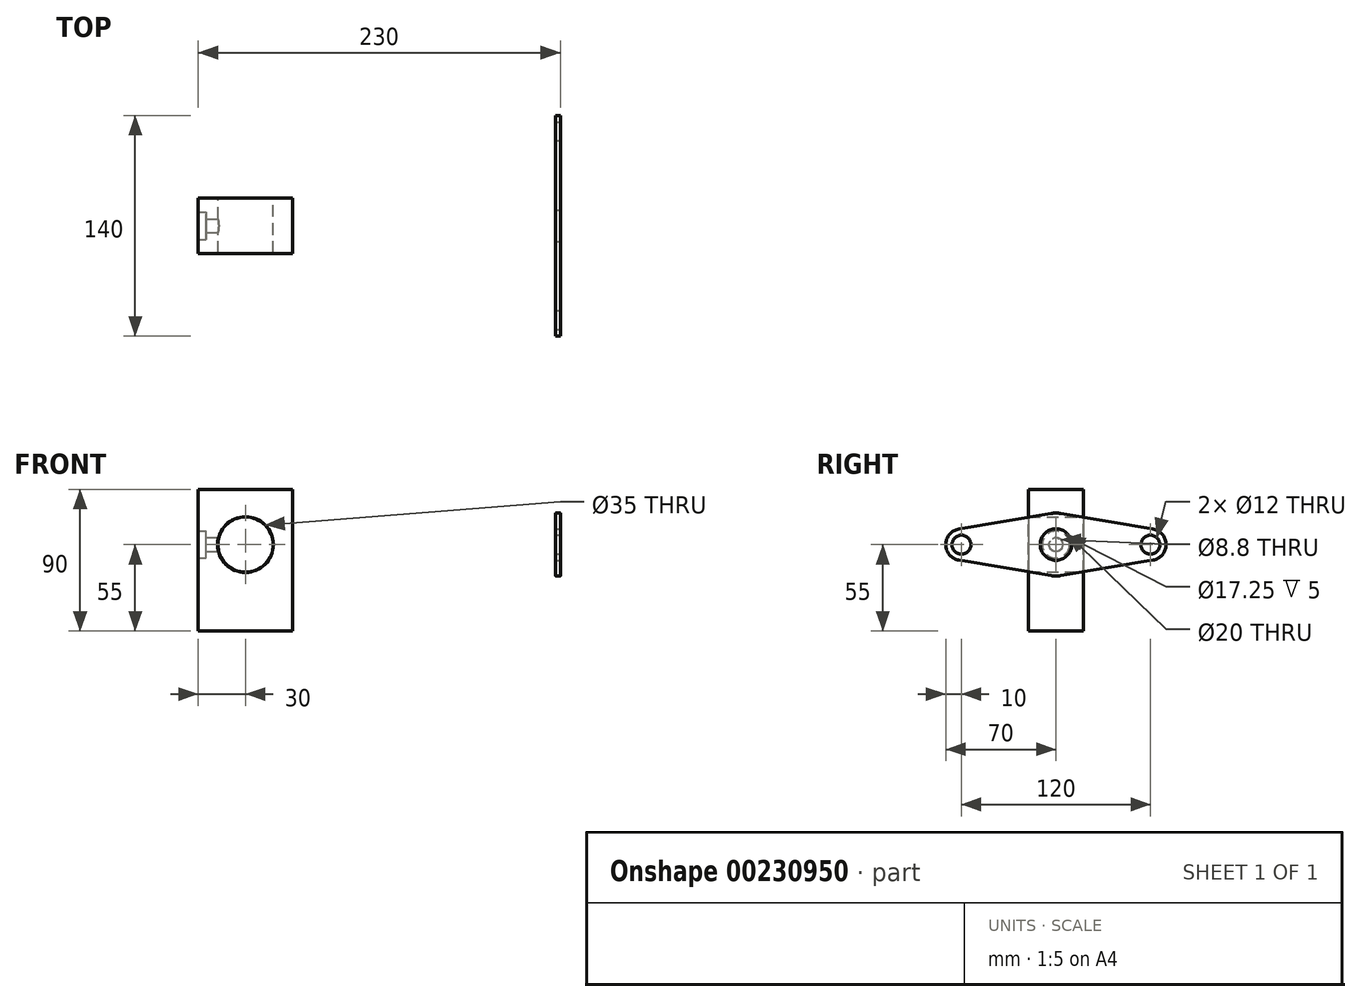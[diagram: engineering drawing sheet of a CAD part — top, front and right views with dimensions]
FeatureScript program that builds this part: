
annotation { "Feature Type Name" : "Feature", "Feature Type Description" : "" }
export const myFeature = defineFeature(function(context is Context, id is Id, definition is map)
    precondition{}
    {
        {
            var Q0;
            Q0=qCreatedBy(makeId("Front.planeOp"),FACE);
            var sketch = newSketch(context, id + "F0", { "sketchPlane" : qUnion([Q0])});
            skCircle(sketch, "E0", {"center": v(0, 0) * mm, "radius": 125 * mm, "construction": true});
            skLineSegment(sketch, "E1", {"start": v(-224.12, 0) * mm, "end": v(217.68, 0) * mm, "construction": true});
            skLineSegment(sketch, "E2", {"start": v(-200, 15.88) * mm, "end": v(-200, -15.88) * mm, "construction": true});
            skLineSegment(sketch, "E3", {"start": v(200, 15.88) * mm, "end": v(200, -15.88) * mm, "construction": true});
            skCircle(sketch, "E4", {"center": v(-200, 0) * mm, "radius": 17.5 * mm});
            skPoint(sketch, "E4.centerSnap0", {"position": v(-200, 0) * mm});
            skLineSegment(sketch, "E5.bottom", {"start": v(-230, 35) * mm, "end": v(-170, 35) * mm});
            skLineSegment(sketch, "E5.top", {"start": v(-230, -55) * mm, "end": v(-170, -55) * mm});
            skLineSegment(sketch, "E5.left", {"start": v(-230, 35) * mm, "end": v(-230, -55) * mm});
            skLineSegment(sketch, "E5.right", {"start": v(-170, 35) * mm, "end": v(-170, -55) * mm});
            skSolve(sketch);
        }
        {
            var Q0;
            Q0 = qSketchRegion(id + "F0", true);
            extrude(context, id + "F1", {"entities" : qUnion([Q0]), "depth" : 35 * mm, "symmetric" : true});
        }
        {
            var Q0;
            Q0=makeQuery(id+"F1.opExtrude","SWEPT_FACE",FACE,{"disambiguationData":[OSD([sQuery(id+"F0.wireOp",EDGE,"E5.left")])]});
            var sketch = newSketch(context, id + "F2", { "sketchPlane" : qUnion([Q0])});
            skLineSegment(sketch, "E6", {"start": v(0, 50.85) * mm, "end": v(0, -62.77) * mm, "construction": true});
            skPoint(sketch, "E6.endSnap0", {"position": v(0, -55) * mm});
            skLineSegment(sketch, "E7", {"start": v(-23.54, 0) * mm, "end": v(23.25, 0) * mm, "construction": true});
            skPoint(sketch, "E8", {"position": v(0, 0) * mm});
            skSolve(sketch);
        }
        {
            var Q0;
            Q0=sQuery(id+"F2.wireOp",VERTEX,"E8");
            var Q1;
            Q1=makeQuery(id+"F1.opExtrude","SWEPT_BODY",BODY,{"disambiguationData":[OSD([sQuery(id+"F0.wireOp",EDGE,"E4"),sQuery(id+"F0.wireOp",EDGE,"E5.bottom"),sQuery(id+"F0.wireOp",EDGE,"E5.top"),sQuery(id+"F0.wireOp",EDGE,"E5.left"),sQuery(id+"F0.wireOp",EDGE,"E5.right")])]});
            hole(context, id + "F3", {"style" : HoleStyle.C_BORE, "endStyle" : HoleEndStyle.BLIND, "holeDiameter" : 8.8 * mm, "cBoreDiameter" : 17.25 * mm, "cBoreDepth" : 5 * mm, "holeDepth" : 15 * mm, "locations" : qUnion([Q0]), "scope" : qUnion([Q1]), "startStyle" : HoleStartStyle.SKETCH});
        }
        {
            var Q0;
            Q0=makeQuery(id+"F3.hole-0.boolean.opBoolean","COPY",EDGE,{"derivedFrom":makeQuery(id+"F3.hole-0.opRevolve","SWEPT_EDGE",EDGE,{"disambiguationData":[OSD([sQuery(id+"F3.hole-0.sketch.wireOp",EDGE,"cbore_start_line_2"),sQuery(id+"F3.hole-0.sketch.wireOp",EDGE,"cbore_start_line_3")])]})});
            var Q1;
            Q1=makeQuery(id+"F1.opExtrude","CAP_EDGE",EDGE,{"disambiguationData":[OSD([sQuery(id+"F0.wireOp",EDGE,"E4")])],"isStart":false});
            var Q2;
            Q2=makeQuery(id+"F1.opExtrude","CAP_EDGE",EDGE,{"disambiguationData":[OSD([sQuery(id+"F0.wireOp",EDGE,"E4")])],"isStart":true});
            chamfer(context, id + "F4", {"entities" : qUnion([Q0, Q1, Q2]), "width" : 0.2 * mm, "tangentPropagation" : true});
        }
        {
            var Q0;
            Q0=qCreatedBy(makeId("Right.planeOp"),FACE);
            var sketch = newSketch(context, id + "F5", { "sketchPlane" : qUnion([Q0])});
            skArc(sketch, "E9", {"start": v(3.33, 19.72) * mm, "mid": v(0, 20) * mm, "end": v(-3.33, 19.72) * mm});
            skArc(sketch, "E10", {"start": v(-61.67, 9.86) * mm, "mid": v(-70, 0) * mm, "end": v(-61.67, -9.86) * mm});
            skArc(sketch, "E11", {"start": v(61.67, -9.86) * mm, "mid": v(70, 0) * mm, "end": v(61.67, 9.86) * mm});
            skLineSegment(sketch, "E12", {"start": v(61.67, 9.86) * mm, "end": v(3.33, 19.72) * mm});
            skLineSegment(sketch, "E13", {"start": v(-61.67, 9.86) * mm, "end": v(-3.33, 19.72) * mm});
            skLineSegment(sketch, "E14", {"start": v(61.67, -9.86) * mm, "end": v(3.33, -19.72) * mm});
            skLineSegment(sketch, "E15", {"start": v(-61.67, -9.86) * mm, "end": v(-3.33, -19.72) * mm});
            skArc(sketch, "E16.trimOffspring", {"start": v(-3.33, -19.72) * mm, "mid": v(0, -20) * mm, "end": v(3.33, -19.72) * mm});
            skCircle(sketch, "E17", {"center": v(0, 0) * mm, "radius": 10 * mm});
            skCircle(sketch, "E18", {"center": v(60, 0) * mm, "radius": 6 * mm});
            skCircle(sketch, "E19", {"center": v(-60, 0) * mm, "radius": 6 * mm});
            skSolve(sketch);
        }
        {
            var Q0;
            Q0=makeQuery(id+"F5.imprint","IMPRINT",FACE,{"disambiguationData":[TD([[makeQuery(id+"F5.imprint","IMPRINT",EDGE,{"derivedFrom":sQuery(id+"F5.wireOp",EDGE,"E9")}),1.0]])]});
            extrude(context, id + "F6", {"entities" : qUnion([Q0]), "oppositeDirection" : true, "depth" : 3 * mm});
        }
    });
